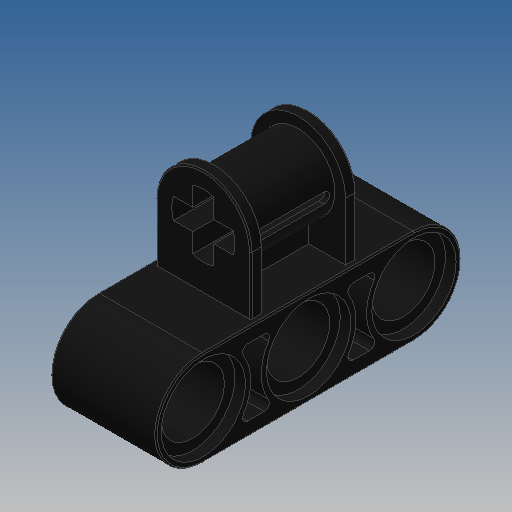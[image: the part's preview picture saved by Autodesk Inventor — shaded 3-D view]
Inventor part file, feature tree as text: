
AUTODESK INVENTOR PART (.ipt)
format: ipt  version: 2022.2 (Build 262287000, 287)  size: 338,432 bytes
history: native  units: in
note: dims shown in document units (in); Inventor stores cm internally (conversion verified against a paired STEP export)
features: extrude x6, sketch x5, mirror x2, fillet x1
ambient origin geometry x8: Origin, YZ Plane, XZ Plane, XY Plane, X Axis, Y Axis, Z Axis, Center Point
bodies: Solid1 (feature_tree)
feature tree (14):
  extrude  "Extrusion1"  Depth=0.315in
  sketch  "Sketch8"  dims[d23=0.0315in d24=0.2205in d25=0.315in d26=0.0in d29=0.0315in d30=0.0in d39=0.0039in d40=0.315in d41=0.2835in d43=0.2835in d44=0.252in d45=0.0315in d46=0.0in d48=45.0deg d49=0.0945in d50=0.0in d51=0.0157in]
  extrude  "Extrusion5"  Depth=0.2205in
  extrude  "Extrusion6"  Depth=0.189in
  mirror  "Mirror2"
  extrude  "Extrusion2"  Depth=0.315in TaperAngle=0.0deg
  extrude  "Extrusion3"  Depth=0.2205in
  extrude  "Extrusion4"  Depth=0.315in TaperAngle=0.0deg
  mirror  "Mirror1"
  fillet  "Fillet1"  Radius=0.0315in
  sketch  "Sketch2"  dims[d0=0.189in d2=0.315in]
  sketch  "Sketch4"  dims[d3=0.315in d4=0.0in d12=0.2205in]
  sketch  "Sketch5"  dims[d14=0.063in d18=0.189in]
  sketch  "Sketch6"  dims[d20=0.063in d21=0.315in d22=0.0in]
